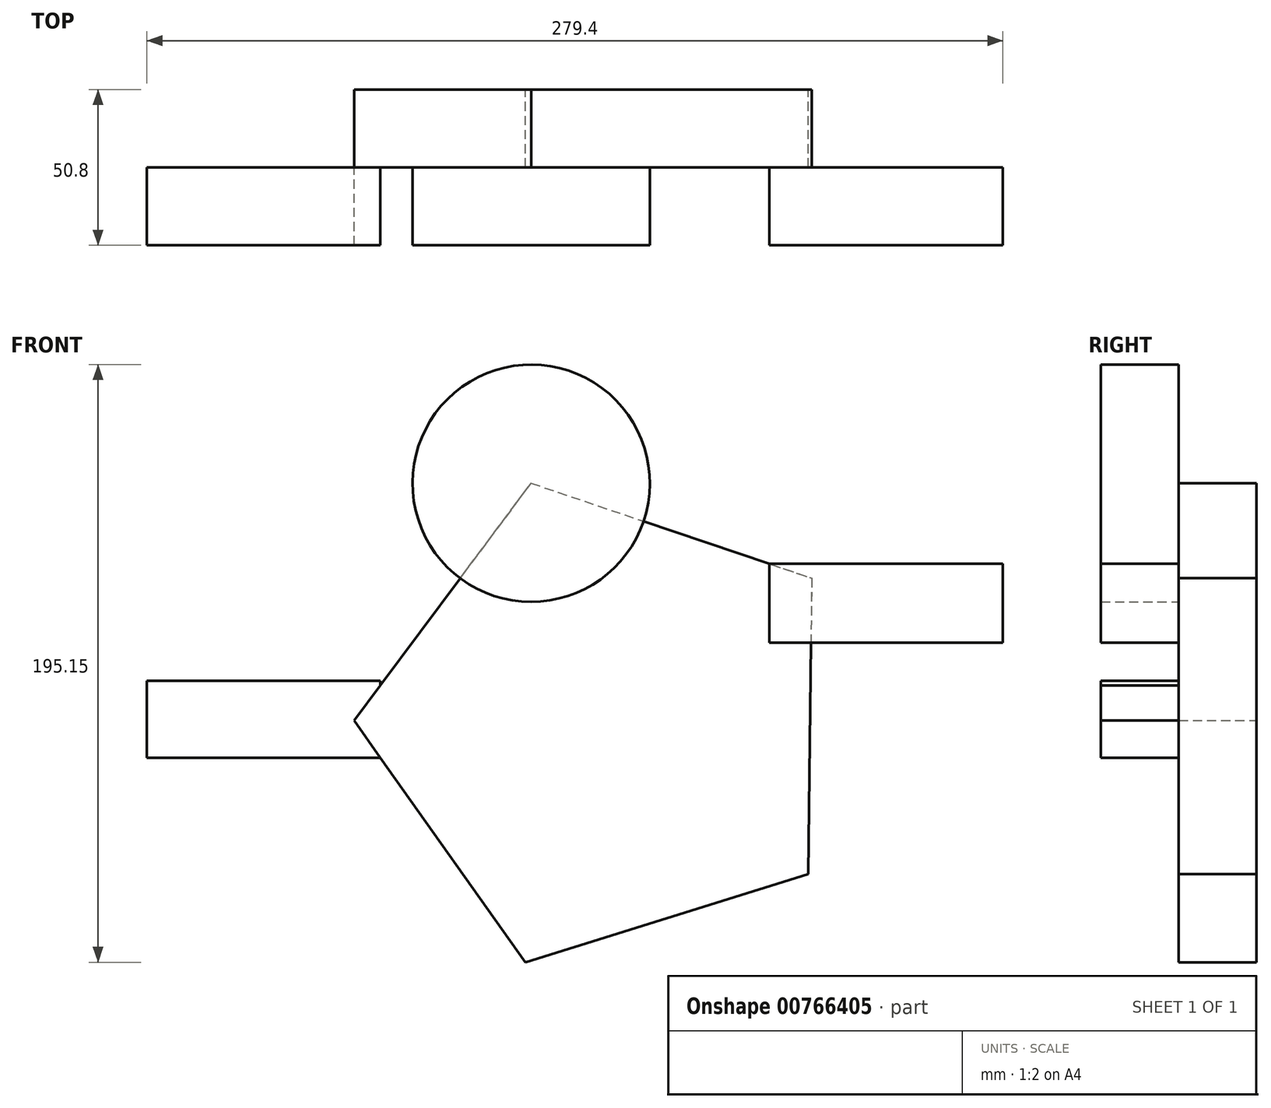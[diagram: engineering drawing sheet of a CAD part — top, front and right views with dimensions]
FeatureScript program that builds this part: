
annotation { "Feature Type Name" : "Feature", "Feature Type Description" : "" }
export const myFeature = defineFeature(function(context is Context, id is Id, definition is map)
    precondition{}
    {
        {
            var Q0;
            Q0=qCreatedBy(makeId("Front.planeOp"),FACE);
            var sketch = newSketch(context, id + "F0", { "sketchPlane" : qUnion([Q0])});
            skCircle(sketch, "E0.cCircle", {"center": v(-28.03, 3.82) * mm, "radius": 66.53 * mm, "construction": true});
            skLineSegment(sketch, "E0.0", {"start": v(-54.4, -74.08) * mm, "end": v(-110.26, 4.83) * mm});
            skLineSegment(sketch, "E0.1", {"start": v(-110.26, 4.83) * mm, "end": v(-52.48, 82.34) * mm});
            skLineSegment(sketch, "E0.2", {"start": v(-52.48, 82.34) * mm, "end": v(39.1, 51.34) * mm});
            skLineSegment(sketch, "E0.3", {"start": v(39.1, 51.34) * mm, "end": v(37.91, -45.33) * mm});
            skLineSegment(sketch, "E0.4", {"start": v(37.91, -45.33) * mm, "end": v(-54.4, -74.08) * mm});
            skPoint(sketch, "E0.0.midPoint", {"position": v(-82.33, -34.63) * mm});
            skSolve(sketch);
        }
        {
            var Q0;
            Q0=makeQuery(id+"F0.imprint","IMPRINT",FACE,{"disambiguationData":[TD([[makeQuery(id+"F0.imprint","IMPRINT",EDGE,{"derivedFrom":sQuery(id+"F0.wireOp",EDGE,"E0.0")}),-1.0]])]});
            extrude(context, id + "F1", {"entities" : qUnion([Q0]), "depth" : 25.4 * mm, "offsetDistance" : 25.4 * mm});
        }
        {
            var Q0;
            Q0=makeQuery(id+"F1.opExtrude","CAP_FACE",FACE,{"disambiguationData":[OSD([sQuery(id+"F0.wireOp",EDGE,"E0.0"),sQuery(id+"F0.wireOp",EDGE,"E0.1"),sQuery(id+"F0.wireOp",EDGE,"E0.2"),sQuery(id+"F0.wireOp",EDGE,"E0.3"),sQuery(id+"F0.wireOp",EDGE,"E0.4")])],"isStart":false});
            var sketch = newSketch(context, id + "F2", { "sketchPlane" : qUnion([Q0])});
            skCircle(sketch, "E1", {"center": v(-52.48, 82.34) * mm, "radius": 38.73 * mm});
            skSolve(sketch);
        }
        {
            var Q0;
            {var subQ0=sQuery(id+"F2.wireOp",EDGE,"E1");var subQ1=makeQuery(id+"F1.opExtrude","CAP_EDGE",EDGE,{"disambiguationData":[OSD([sQuery(id+"F0.wireOp",EDGE,"E0.1")])],"isStart":false});var subQ2=makeQuery(id+"F2.imprint","INTERSECT",VERTEX,{"derivedFrom":[subQ1,subQ0]});Q0=makeQuery(id+"F2.imprint","IMPRINT",FACE,{"disambiguationData":[TD([[makeQuery(id+"F2.imprint","IMPRINT",EDGE,{"disambiguationData":[TD([[subQ2,1.0]])],"derivedFrom":subQ0}),1.0]])]});}
            var Q1;
            {var subQ0=sQuery(id+"F2.wireOp",EDGE,"E1");var subQ1=makeQuery(id+"F1.opExtrude","CAP_EDGE",EDGE,{"disambiguationData":[OSD([sQuery(id+"F0.wireOp",EDGE,"E0.1")])],"isStart":false});var subQ2=makeQuery(id+"F2.imprint","INTERSECT",VERTEX,{"derivedFrom":[subQ1,subQ0]});Q1=makeQuery(id+"F2.imprint","IMPRINT",FACE,{"disambiguationData":[TD([[makeQuery(id+"F2.imprint","IMPRINT",EDGE,{"disambiguationData":[TD([[subQ2,-1.0]])],"derivedFrom":subQ0}),1.0]])]});}
            extrude(context, id + "F3", {"entities" : qUnion([Q0, Q1]), "operationType" : NewBodyOperationType.ADD, "depth" : 25.4 * mm, "offsetDistance" : 25.4 * mm});
        }
        {
            var Q0;
            Q0=makeQuery(id+"F1.opExtrude","CAP_FACE",FACE,{"disambiguationData":[OSD([sQuery(id+"F0.wireOp",EDGE,"E0.0"),sQuery(id+"F0.wireOp",EDGE,"E0.1"),sQuery(id+"F0.wireOp",EDGE,"E0.2"),sQuery(id+"F0.wireOp",EDGE,"E0.3"),sQuery(id+"F0.wireOp",EDGE,"E0.4")])],"isStart":false});
            var sketch = newSketch(context, id + "F4", { "sketchPlane" : qUnion([Q0])});
            skLineSegment(sketch, "E2.bottom", {"start": v(-101.68, -7.3) * mm, "end": v(-177.88, -7.3) * mm});
            skLineSegment(sketch, "E2.top", {"start": v(-101.68, 17.81) * mm, "end": v(-177.88, 17.81) * mm});
            skLineSegment(sketch, "E2.left", {"start": v(-101.68, -7.3) * mm, "end": v(-101.68, 17.81) * mm});
            skLineSegment(sketch, "E2.right", {"start": v(-177.88, -7.3) * mm, "end": v(-177.88, 17.81) * mm});
            skLineSegment(sketch, "E3.bottom", {"start": v(-177.88, 17.81) * mm, "end": v(-181.24, 17.81) * mm});
            skLineSegment(sketch, "E3.top", {"start": v(-177.88, 29.6) * mm, "end": v(-181.24, 29.6) * mm});
            skLineSegment(sketch, "E3.left", {"start": v(-177.88, 17.81) * mm, "end": v(-177.88, 29.6) * mm});
            skLineSegment(sketch, "E3.right", {"start": v(-181.24, 17.81) * mm, "end": v(-181.24, 29.6) * mm});
            skSolve(sketch);
        }
        {
            var Q0;
            {var subQ5=sQuery(id+"F4.wireOp",EDGE,"E2.bottom");Q0=makeQuery(id+"F4.imprint","IMPRINT",FACE,{"disambiguationData":[TD([[makeQuery(id+"F4.imprint","IMPRINT",EDGE,{"derivedFrom":subQ5}),-1.0]])]});}
            extrude(context, id + "F5", {"entities" : qUnion([Q0]), "depth" : 25.4 * mm, "offsetDistance" : 25.4 * mm});
        }
        {
            var Q0;
            Q0=makeQuery(id+"F1.opExtrude","CAP_FACE",FACE,{"disambiguationData":[OSD([sQuery(id+"F0.wireOp",EDGE,"E0.0"),sQuery(id+"F0.wireOp",EDGE,"E0.1"),sQuery(id+"F0.wireOp",EDGE,"E0.2"),sQuery(id+"F0.wireOp",EDGE,"E0.3"),sQuery(id+"F0.wireOp",EDGE,"E0.4")])],"isStart":false});
            var sketch = newSketch(context, id + "F6", { "sketchPlane" : qUnion([Q0])});
            skLineSegment(sketch, "E4.bottom", {"start": v(25.32, 56) * mm, "end": v(101.52, 56) * mm});
            skLineSegment(sketch, "E4.top", {"start": v(25.32, 30.26) * mm, "end": v(101.52, 30.26) * mm});
            skLineSegment(sketch, "E4.left", {"start": v(25.32, 56) * mm, "end": v(25.32, 30.26) * mm});
            skLineSegment(sketch, "E4.right", {"start": v(101.52, 56) * mm, "end": v(101.52, 30.26) * mm});
            skSolve(sketch);
        }
        {
            var Q0;
            {var subQ8=sQuery(id+"F6.wireOp",EDGE,"E4.bottom");Q0=makeQuery(id+"F6.imprint","IMPRINT",FACE,{"disambiguationData":[TD([[makeQuery(id+"F6.imprint","IMPRINT",EDGE,{"derivedFrom":subQ8}),-1.0]])]});}
            var Q1;
            {var subQ0=sQuery(id+"F6.wireOp",EDGE,"E4.left");Q1=makeQuery(id+"F6.imprint","IMPRINT",FACE,{"disambiguationData":[TD([[makeQuery(id+"F6.imprint","IMPRINT",EDGE,{"derivedFrom":subQ0}),1.0]])]});}
            extrude(context, id + "F7", {"entities" : qUnion([Q0, Q1]), "operationType" : NewBodyOperationType.ADD, "depth" : 25.4 * mm, "offsetDistance" : 25.4 * mm});
        }
    });
